# Revit family: 7Automatic Lavatory Faucet_TOTO_TLP01701
name_source: partatom
category: 衛生器具
revit_build: Autodesk Revit 2018 (Build: 20181011_1500(x64)
units: mm (PartAtom-declared; Revit-internal decimal feet)

## family parameters
OmniClass タイトル = Sanitary, Laundry, and Cleaning Equipment
OmniClass 番号 = 23.45.00.00
パーツ タイプ = 標準
ロード時にボイドで切り取り = いいえ
丸型コネクタ寸法 = 直径を使用
作業面ベース = いいえ
共有 = いいえ
常に垂直 = はい
部屋計算ポイント = いいえ

## types (1)
- 7Automatic Lavatory Faucet_TOTO_TLP01701
    Chrome = Chrome
    Height = 236
    TOTO asiaoceania = TLP01701J /
    TOTO asiaoceania URL = http://asia.toto.com
    TOTO china = TLP01701J
    TOTO china URL = http://www.toto.com.cn
    TOTO europe = TLP01701G
    TOTO europe URL = https://gb.toto.com
    TOTO hongkong = TLP01701J
    TOTO hongkong URL = http://hk.toto.com
    TOTO india = TLP01701J
    TOTO india URL = https://in.toto.com
    TOTO taiwan 1 = TLP01701P-S1
    TOTO taiwan 2 = TLP01701P-S
    TOTO taiwan URL 1 = https://www.twtoto.com.tw
    TOTO taiwan URL 2 = https://www.twtoto.com.tw
    TOTO thailand = TLP01701T
    TOTO thailand URL = https://th.toto.com
    TOTO usa = TLP01701U
    TOTO usa URL = https://www.totousa.com
    TOTO vietnam = TLP01701J
    製造元 = TOTO LTD.
    説明 = Automatic Lavatory Faucet
